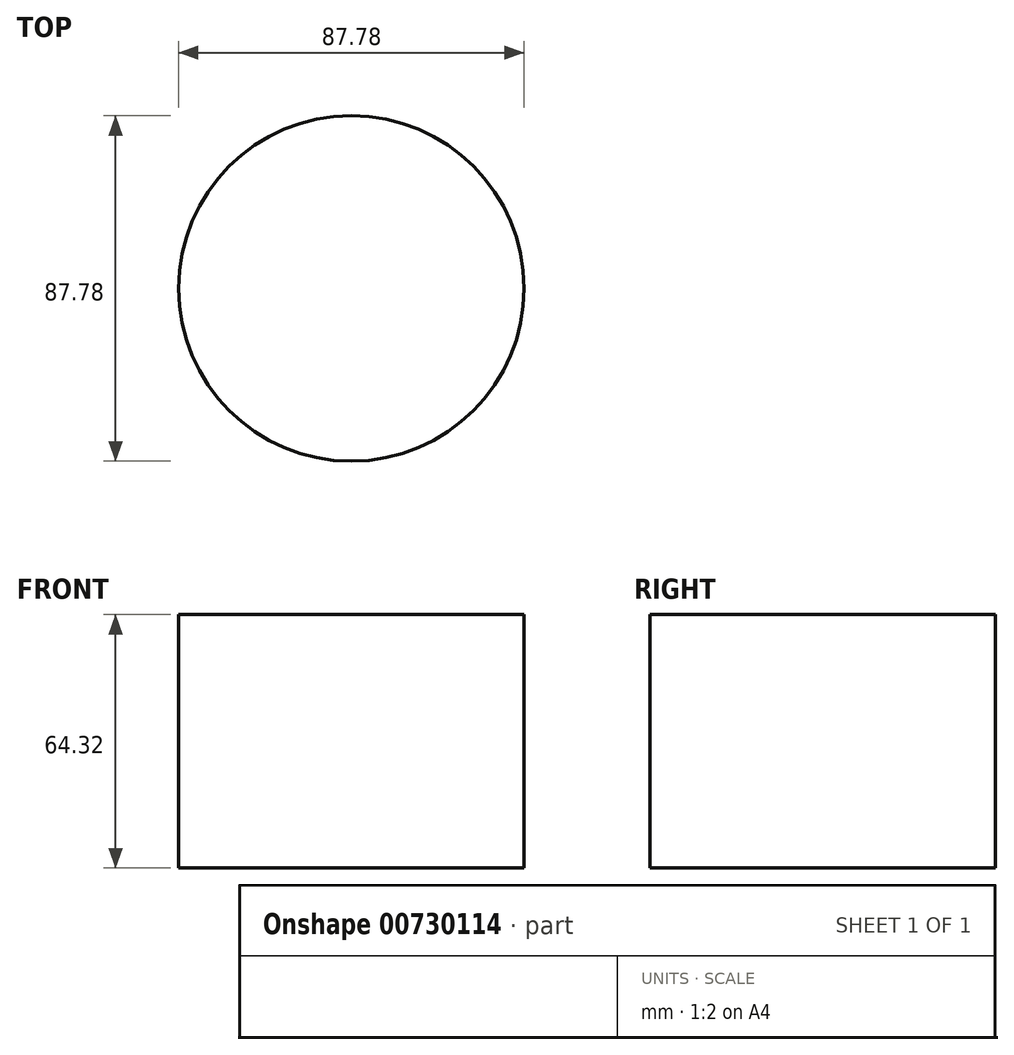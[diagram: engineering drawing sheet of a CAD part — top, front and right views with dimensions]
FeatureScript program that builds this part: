
annotation { "Feature Type Name" : "Feature", "Feature Type Description" : "" }
export const myFeature = defineFeature(function(context is Context, id is Id, definition is map)
    precondition{}
    {
        {
            var Q0;
            Q0=qCreatedBy(makeId("Front.planeOp"),FACE);
            var sketch = newSketch(context, id + "F0", { "sketchPlane" : qUnion([Q0])});
            skLineSegment(sketch, "E0.bottom", {"start": v(0, 0) * mm, "end": v(-43.9, 0) * mm});
            skLineSegment(sketch, "E0.top", {"start": v(0, 64.32) * mm, "end": v(-43.9, 64.32) * mm});
            skLineSegment(sketch, "E0.left", {"start": v(0, 0) * mm, "end": v(0, 64.32) * mm});
            skLineSegment(sketch, "E0.right", {"start": v(-43.9, 0) * mm, "end": v(-43.9, 64.32) * mm});
            skSolve(sketch);
        }
        {
            var Q0;
            Q0=makeQuery(id+"F0.imprint","IMPRINT",FACE,{"disambiguationData":[TD([[makeQuery(id+"F0.imprint","IMPRINT",EDGE,{"derivedFrom":sQuery(id+"F0.wireOp",EDGE,"E0.bottom")}),-1.0]])]});
            var Q1;
            Q1=sQuery(id+"F0.wireOp",EDGE,"E0.left");
            revolve(context, id + "F1", {"surfaceOperationType" : NewSurfaceOperationType.NEW, "entities" : qUnion([Q0]), "axis" : qUnion([Q1]), "revolveType" : RevolveType.FULL});
        }
    });
